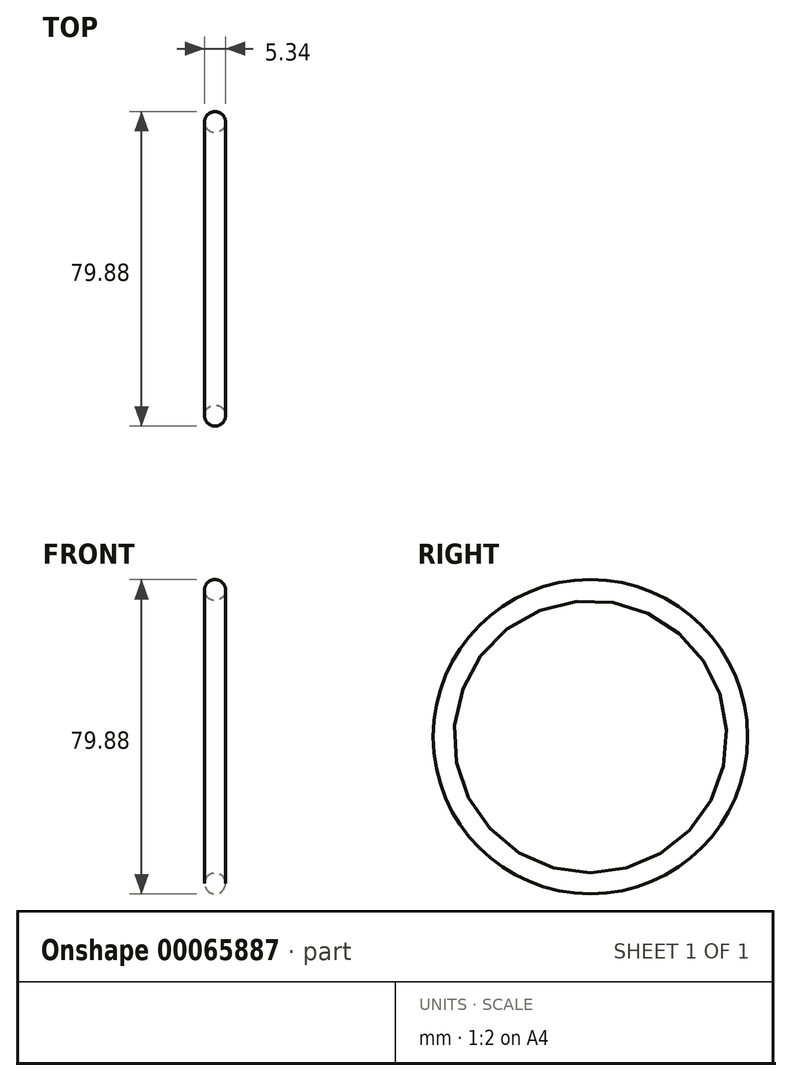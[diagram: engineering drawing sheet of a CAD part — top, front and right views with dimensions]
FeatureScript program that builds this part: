
annotation { "Feature Type Name" : "Feature", "Feature Type Description" : "" }
export const myFeature = defineFeature(function(context is Context, id is Id, definition is map)
    precondition{}
    {
        {
            var Q0;
            Q0=qCreatedBy(makeId("Front.planeOp"),FACE);
            var sketch = newSketch(context, id + "F0", { "sketchPlane" : qUnion([Q0])});
            skLineSegment(sketch, "E0", {"start": v(0, 0) * mm, "end": v(-6.06, 0) * mm, "construction": true});
            skCircle(sketch, "E1", {"center": v(0, 37.27) * mm, "radius": 2.67 * mm});
            skSolve(sketch);
        }
        {
            var Q0;
            Q0=makeQuery(id+"F0.imprint","IMPRINT",FACE,{"disambiguationData":[TD([[makeQuery(id+"F0.imprint","IMPRINT",EDGE,{"derivedFrom":sQuery(id+"F0.wireOp",EDGE,"E1")}),1.0]])]});
            var Q1;
            Q1=sQuery(id+"F0.wireOp",EDGE,"E0");
            revolve(context, id + "F1", {"entities" : qUnion([Q0]), "axis" : qUnion([Q1]), "revolveType" : RevolveType.FULL});
        }
    });
